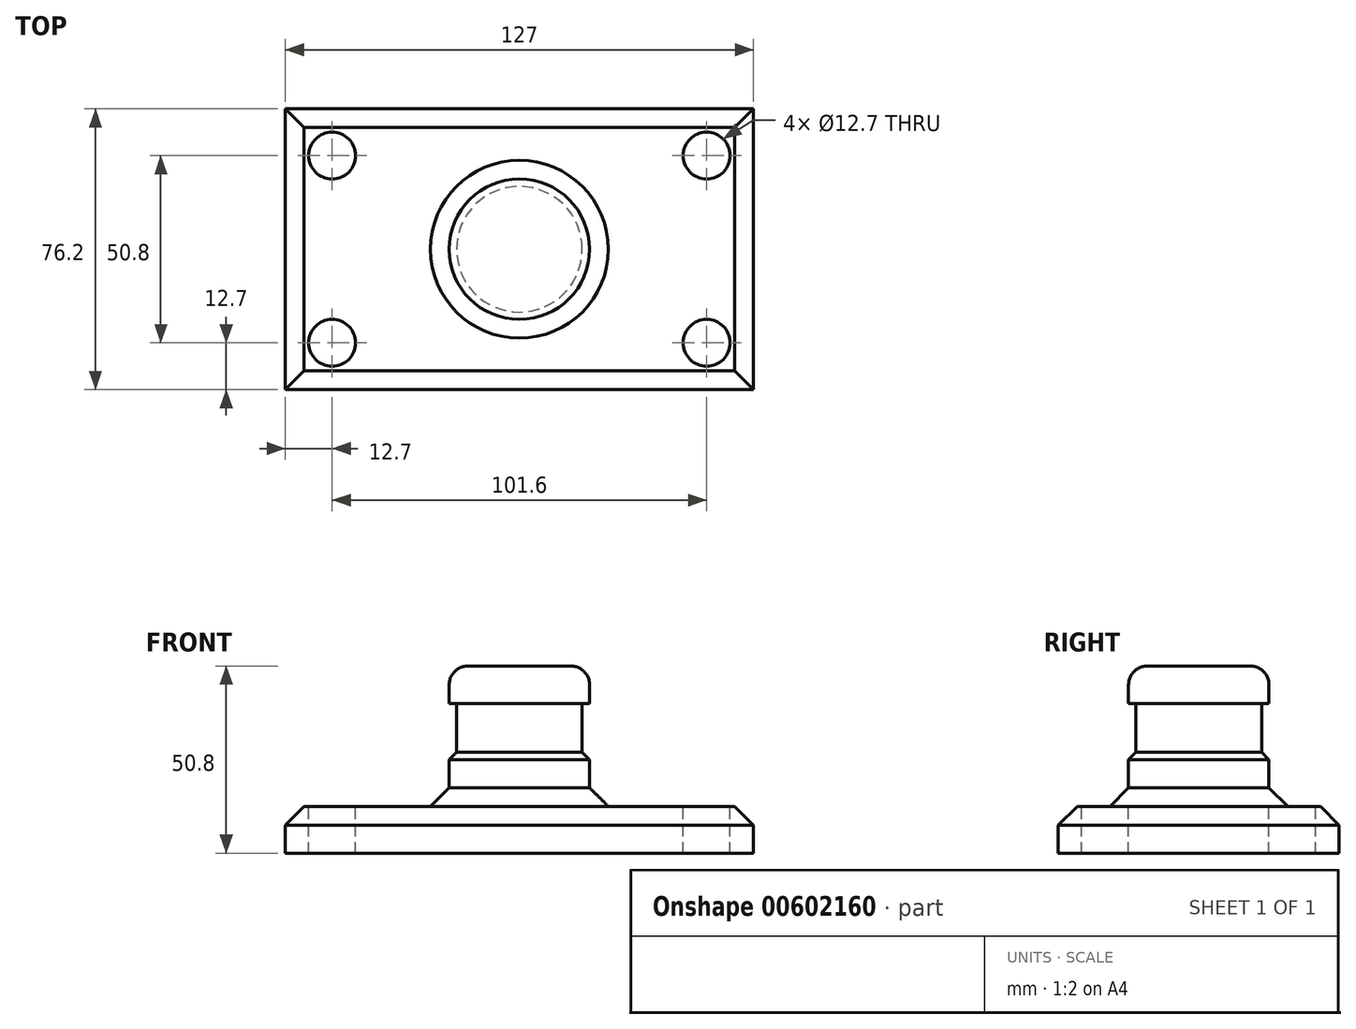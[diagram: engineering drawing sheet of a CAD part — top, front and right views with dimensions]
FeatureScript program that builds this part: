
annotation { "Feature Type Name" : "Feature", "Feature Type Description" : "" }
export const myFeature = defineFeature(function(context is Context, id is Id, definition is map)
    precondition{}
    {
        {
            var Q0;
            Q0=qCreatedBy(makeId("Top.planeOp"),FACE);
            var sketch = newSketch(context, id + "F0", { "sketchPlane" : qUnion([Q0])});
            skLineSegment(sketch, "E0.bottom", {"start": v(63.5, 38.1) * mm, "end": v(-63.5, 38.1) * mm});
            skLineSegment(sketch, "E0.top", {"start": v(63.5, -38.1) * mm, "end": v(-63.5, -38.1) * mm});
            skLineSegment(sketch, "E0.left", {"start": v(63.5, 38.1) * mm, "end": v(63.5, -38.1) * mm});
            skLineSegment(sketch, "E0.right", {"start": v(-63.5, 38.1) * mm, "end": v(-63.5, -38.1) * mm});
            skPoint(sketch, "E0.middle", {"position": v(0, 0) * mm});
            skSolve(sketch);
        }
        {
            var Q0;
            Q0=makeQuery(id+"F0.imprint","IMPRINT",FACE,{"disambiguationData":[TD([[makeQuery(id+"F0.imprint","IMPRINT",EDGE,{"derivedFrom":sQuery(id+"F0.wireOp",EDGE,"E0.bottom")}),1.0]])]});
            extrude(context, id + "F1", {"entities" : qUnion([Q0]), "depth" : 12.7 * mm, "offsetDistance" : 25.4 * mm});
        }
        {
            var Q0;
            Q0=makeQuery(id+"F1.opExtrude","CAP_FACE",FACE,{"disambiguationData":[OSD([sQuery(id+"F0.wireOp",EDGE,"E0.bottom"),sQuery(id+"F0.wireOp",EDGE,"E0.top"),sQuery(id+"F0.wireOp",EDGE,"E0.left"),sQuery(id+"F0.wireOp",EDGE,"E0.right")])],"isStart":false});
            var sketch = newSketch(context, id + "F2", { "sketchPlane" : qUnion([Q0])});
            skCircle(sketch, "E1", {"center": v(-50.8, 25.4) * mm, "radius": 6.35 * mm});
            skCircle(sketch, "E2", {"center": v(-50.8, -25.4) * mm, "radius": 6.35 * mm});
            skCircle(sketch, "E3", {"center": v(50.8, 25.4) * mm, "radius": 6.35 * mm});
            skCircle(sketch, "E4", {"center": v(50.8, -25.4) * mm, "radius": 6.35 * mm});
            skSolve(sketch);
        }
        {
            var Q0;
            Q0=makeQuery(id+"F2.imprint","IMPRINT",FACE,{"disambiguationData":[TD([[makeQuery(id+"F2.imprint","IMPRINT",EDGE,{"derivedFrom":sQuery(id+"F2.wireOp",EDGE,"E4")}),1.0]])]});
            var Q1;
            Q1=makeQuery(id+"F2.imprint","IMPRINT",FACE,{"disambiguationData":[TD([[makeQuery(id+"F2.imprint","IMPRINT",EDGE,{"derivedFrom":sQuery(id+"F2.wireOp",EDGE,"E3")}),1.0]])]});
            var Q2;
            Q2=makeQuery(id+"F2.imprint","IMPRINT",FACE,{"disambiguationData":[TD([[makeQuery(id+"F2.imprint","IMPRINT",EDGE,{"derivedFrom":sQuery(id+"F2.wireOp",EDGE,"E1")}),1.0]])]});
            var Q3;
            Q3=makeQuery(id+"F2.imprint","IMPRINT",FACE,{"disambiguationData":[TD([[makeQuery(id+"F2.imprint","IMPRINT",EDGE,{"derivedFrom":sQuery(id+"F2.wireOp",EDGE,"E2")}),1.0]])]});
            extrude(context, id + "F3", {"entities" : qUnion([Q0, Q1, Q2, Q3]), "operationType" : NewBodyOperationType.REMOVE, "endBound" : BoundingType.THROUGH_ALL, "oppositeDirection" : true, "depth" : 25.4 * mm, "offsetDistance" : 25.4 * mm});
        }
        {
            var Q0;
            Q0=qCreatedBy(makeId("Front.planeOp"),FACE);
            var sketch = newSketch(context, id + "F4", { "sketchPlane" : qUnion([Q0])});
            skLineSegment(sketch, "E5.bottom", {"start": v(0, 12.7) * mm, "end": v(19.05, 12.7) * mm});
            skLineSegment(sketch, "E5.top", {"start": v(0, 50.8) * mm, "end": v(19.05, 50.8) * mm});
            skLineSegment(sketch, "E5.left", {"start": v(0, 12.7) * mm, "end": v(0, 50.8) * mm});
            skLineSegment(sketch, "E5.right", {"start": v(19.05, 12.7) * mm, "end": v(19.05, 50.8) * mm});
            skSolve(sketch);
        }
        {
            var Q0;
            Q0=makeQuery(id+"F4.imprint","IMPRINT",FACE,{"disambiguationData":[TD([[makeQuery(id+"F4.imprint","IMPRINT",EDGE,{"derivedFrom":sQuery(id+"F4.wireOp",EDGE,"E5.bottom")}),1.0]])]});
            var Q1;
            Q1=sQuery(id+"F4.wireOp",EDGE,"E5.left");
            revolve(context, id + "F5", {"operationType" : NewBodyOperationType.ADD, "entities" : qUnion([Q0]), "axis" : qUnion([Q1]), "revolveType" : RevolveType.FULL});
        }
        {
            var Q0;
            Q0=qCreatedBy(makeId("Front.planeOp"),FACE);
            var sketch = newSketch(context, id + "F6", { "sketchPlane" : qUnion([Q0])});
            skLineSegment(sketch, "E6.bottom", {"start": v(17.05, 30.48) * mm, "end": v(23.4, 30.48) * mm});
            skLineSegment(sketch, "E6.top", {"start": v(17.05, 40.64) * mm, "end": v(23.4, 40.64) * mm});
            skLineSegment(sketch, "E6.left", {"start": v(17.05, 30.48) * mm, "end": v(17.05, 40.64) * mm});
            skLineSegment(sketch, "E6.right", {"start": v(23.4, 30.48) * mm, "end": v(23.4, 40.64) * mm});
            skSolve(sketch);
        }
        {
            var Q0;
            Q0=makeQuery(id+"F6.imprint","IMPRINT",FACE,{"disambiguationData":[TD([[makeQuery(id+"F6.imprint","IMPRINT",EDGE,{"derivedFrom":sQuery(id+"F6.wireOp",EDGE,"E6.bottom")}),1.0]])]});
            var Q1;
            Q1=makeQuery(id+"F5.opRevolve","SWEPT_EDGE",EDGE,{"disambiguationData":[OSD([sQuery(id+"F4.wireOp",EDGE,"E5.top"),sQuery(id+"F4.wireOp",EDGE,"E5.right")])]});
            revolve(context, id + "F7", {"operationType" : NewBodyOperationType.REMOVE, "entities" : qUnion([Q0]), "axis" : qUnion([Q1]), "revolveType" : RevolveType.FULL, "oppositeDirection" : true});
        }
        {
            var Q0;
            Q0=makeQuery(id+"F5.opRevolve","SWEPT_EDGE",EDGE,{"disambiguationData":[OSD([sQuery(id+"F4.wireOp",EDGE,"E5.top"),sQuery(id+"F4.wireOp",EDGE,"E5.right")])]});
            fillet(context, id + "F8", {"entities" : qUnion([Q0]), "radius" : 5.08 * mm, "tangentPropagation" : true, "allowEdgeOverflow" : false});
        }
        {
            var Q0;
            Q0=makeQuery(id+"F7.boolean.opBoolean","SPLIT",FACE,{"disambiguationData":[TD([makeQuery(id+"F7.opRevolve","SWEPT_FACE",FACE,{"disambiguationData":[OSD([sQuery(id+"F6.wireOp",EDGE,"E6.bottom")])]})])],"derivedFrom":makeQuery(id+"F5.opRevolve","SWEPT_FACE",FACE,{"disambiguationData":[OSD([sQuery(id+"F4.wireOp",EDGE,"E5.right")])]})});
            chamfer(context, id + "F9", {"entities" : qUnion([Q0]), "width" : 5.08 * mm, "tangentPropagation" : true});
        }
        {
            var Q0;
            Q0=makeQuery(id+"F1.opExtrude","CAP_EDGE",EDGE,{"disambiguationData":[OSD([sQuery(id+"F0.wireOp",EDGE,"E0.top")])],"isStart":false});
            var Q1;
            Q1=makeQuery(id+"F1.opExtrude","CAP_EDGE",EDGE,{"disambiguationData":[OSD([sQuery(id+"F0.wireOp",EDGE,"E0.left")])],"isStart":false});
            var Q2;
            Q2=makeQuery(id+"F1.opExtrude","CAP_EDGE",EDGE,{"disambiguationData":[OSD([sQuery(id+"F0.wireOp",EDGE,"E0.bottom")])],"isStart":false});
            var Q3;
            Q3=makeQuery(id+"F1.opExtrude","CAP_EDGE",EDGE,{"disambiguationData":[OSD([sQuery(id+"F0.wireOp",EDGE,"E0.right")])],"isStart":false});
            chamfer(context, id + "F10", {"entities" : qUnion([Q0, Q1, Q2, Q3]), "width" : 5.08 * mm, "tangentPropagation" : true});
        }
    });
